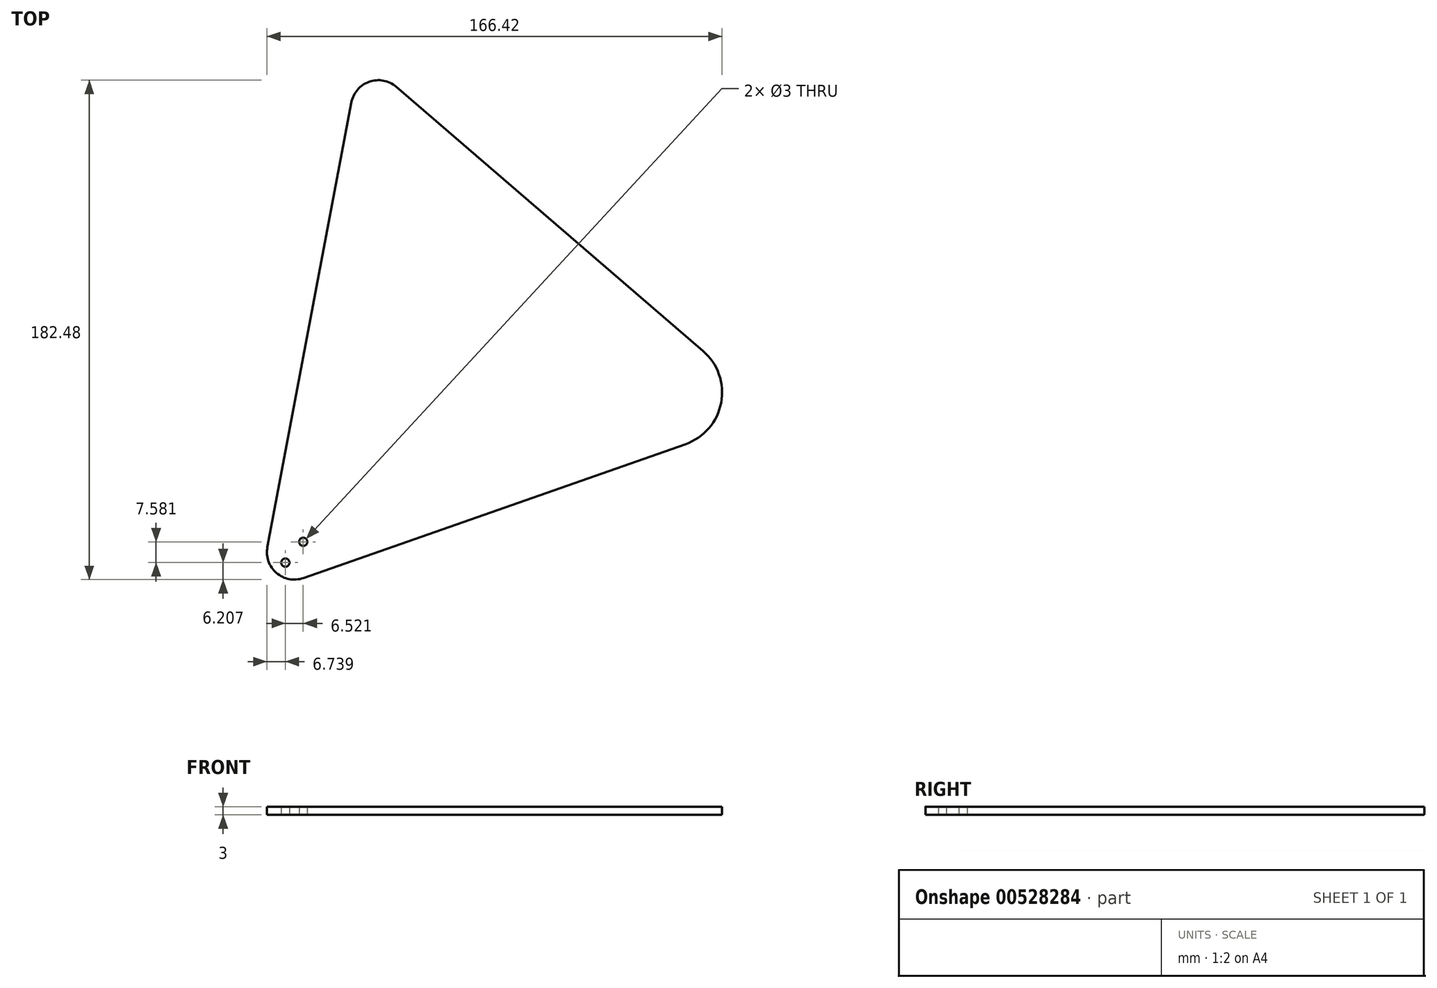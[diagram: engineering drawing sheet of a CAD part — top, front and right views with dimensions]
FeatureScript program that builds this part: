
annotation { "Feature Type Name" : "Feature", "Feature Type Description" : "" }
export const myFeature = defineFeature(function(context is Context, id is Id, definition is map)
    precondition{}
    {
        {
            var Q0;
            Q0=qCreatedBy(makeId("Top.planeOp"),FACE);
            var sketch = newSketch(context, id + "F0", { "sketchPlane" : qUnion([Q0])});
            skLineSegment(sketch, "E0.0", {"start": v(-62.68, 73.75) * mm, "end": v(49.55, -22.8) * mm});
            skLineSegment(sketch, "E0.1", {"start": v(43.12, -56.83) * mm, "end": v(-96.6, -105.75) * mm});
            skLineSegment(sketch, "E0.2", {"start": v(-109.74, -94.45) * mm, "end": v(-79.03, 68.03) * mm});
            skPoint(sketch, "E0.0.midPoint", {"position": v(0, 19.83) * mm});
            skPoint(sketch, "E1.visualSharp", {"position": v(-112.95, -111.47) * mm});
            skArc(sketch, "E1.filletArc", {"start": v(-109.74, -94.45) * mm, "mid": v(-106.43, -103.9) * mm, "end": v(-96.6, -105.75) * mm});
            skPoint(sketch, "E2.visualSharp", {"position": v(-75.81, 85.05) * mm});
            skArc(sketch, "E2.filletArc", {"start": v(-62.68, 73.75) * mm, "mid": v(-72.5, 75.6) * mm, "end": v(-79.03, 68.03) * mm});
            skPoint(sketch, "E3.visualSharp", {"position": v(75.81, -45.38) * mm});
            skArc(sketch, "E3.filletArc", {"start": v(43.12, -56.83) * mm, "mid": v(56.16, -41.67) * mm, "end": v(49.55, -22.8) * mm});
            skCircle(sketch, "E4", {"center": v(-103.17, -100.1) * mm, "radius": 1.5 * mm});
            skCircle(sketch, "E5", {"center": v(-96.65, -92.52) * mm, "radius": 1.5 * mm});
            skSolve(sketch);
        }
        {
            var Q0;
            Q0 = qSketchRegion(id + "F0", true);
            extrude(context, id + "F1", {"entities" : qUnion([Q0]), "depth" : 3 * mm, "offsetDistance" : 25.4 * mm});
        }
    });
